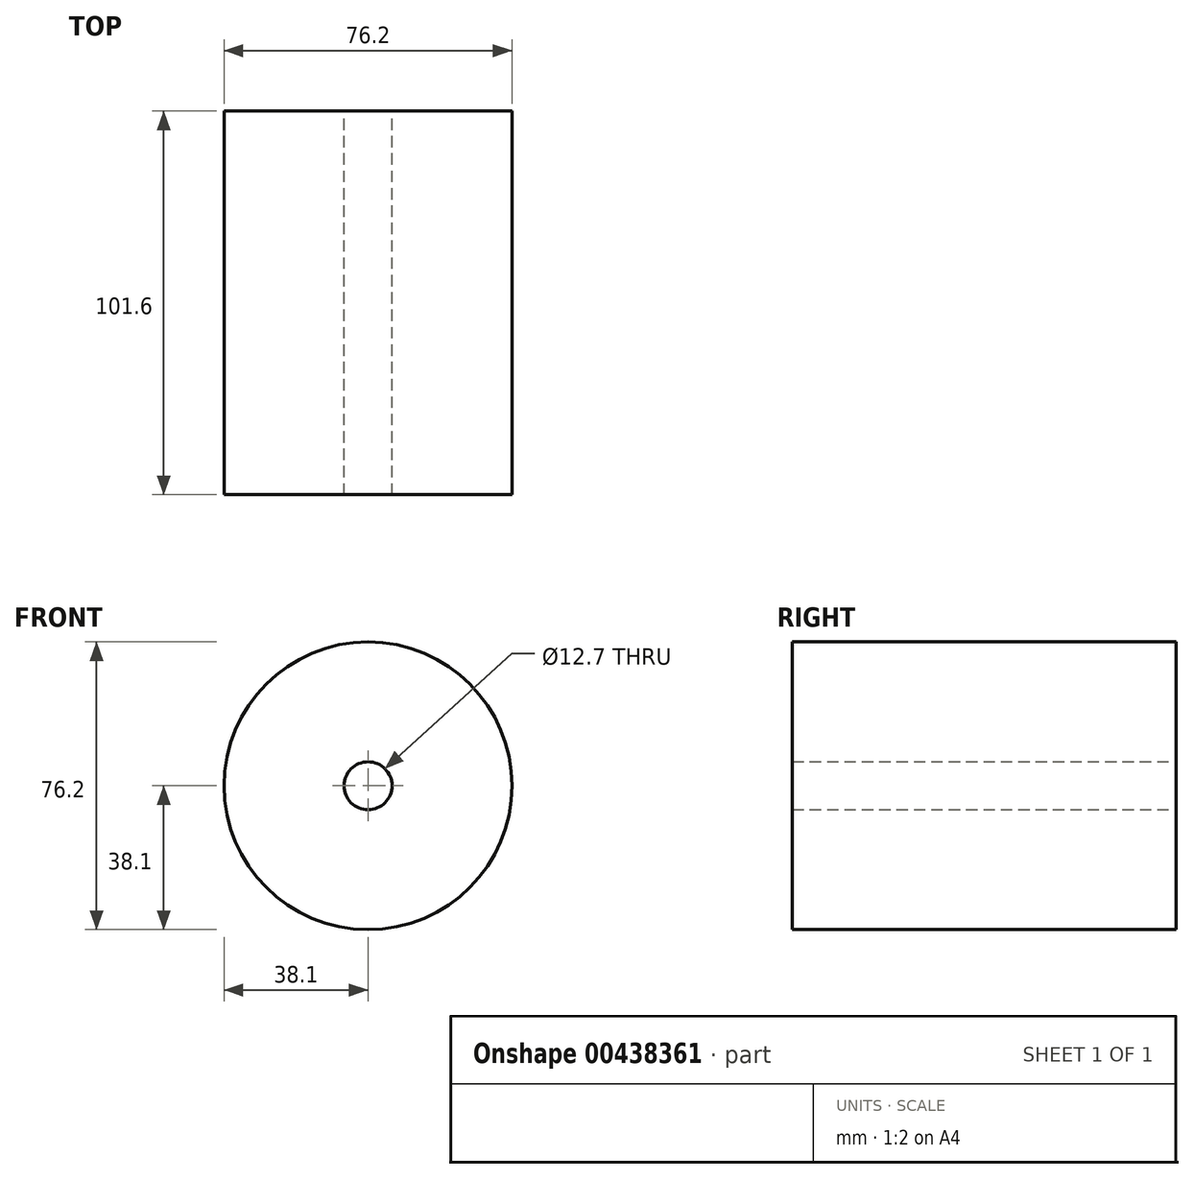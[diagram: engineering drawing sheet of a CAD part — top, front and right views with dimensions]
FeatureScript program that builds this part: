
annotation { "Feature Type Name" : "Feature", "Feature Type Description" : "" }
export const myFeature = defineFeature(function(context is Context, id is Id, definition is map)
    precondition{}
    {
        {
            var Q0;
            Q0=qCreatedBy(makeId("Front.planeOp"),FACE);
            var sketch = newSketch(context, id + "F0", { "sketchPlane" : qUnion([Q0])});
            skCircle(sketch, "E0", {"center": v(0, 0) * mm, "radius": 38.1 * mm});
            skCircle(sketch, "E1", {"center": v(0, 0) * mm, "radius": 6.35 * mm});
            skSolve(sketch);
        }
        {
            var Q0;
            Q0=makeQuery(id+"F0.imprint","IMPRINT",FACE,{"disambiguationData":[TD([[makeQuery(id+"F0.imprint","IMPRINT",EDGE,{"derivedFrom":sQuery(id+"F0.wireOp",EDGE,"E0")}),1.0]])]});
            extrude(context, id + "F1", {"entities" : qUnion([Q0]), "depth" : 101.6 * mm});
        }
    });
